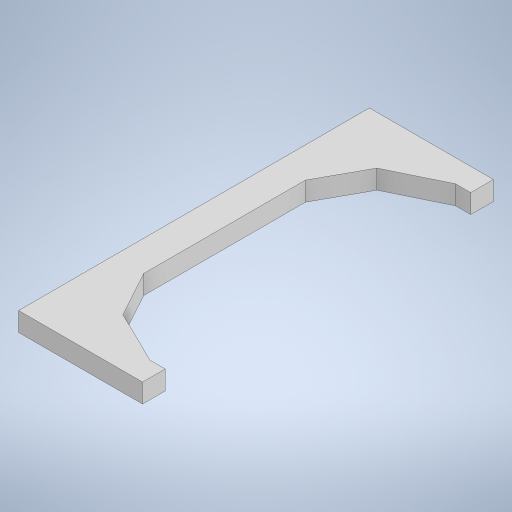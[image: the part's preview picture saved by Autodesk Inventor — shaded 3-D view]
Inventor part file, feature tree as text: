
AUTODESK INVENTOR PART (.ipt)
format: ipt  version: 2024 (Build 280153000, 153)  size: 247,808 bytes
history: native  units: mm
features: extrude x1, mirror x1, sketch x1
ambient origin geometry x8: Origin, YZ Plane, XZ Plane, XY Plane, X Axis, Y Axis, Z Axis, Center Point
bodies: Solid1 (feature_tree)
feature tree (3):
  extrude  "Extrusion1"  Depth=16.0mm
  mirror  "Mirror1"
  sketch  "Sketch1"  dims[d0=65.0mm d1=80.0mm d3=10.0mm d4=0.0mm d5=16.0mm d7=12.0mm]
